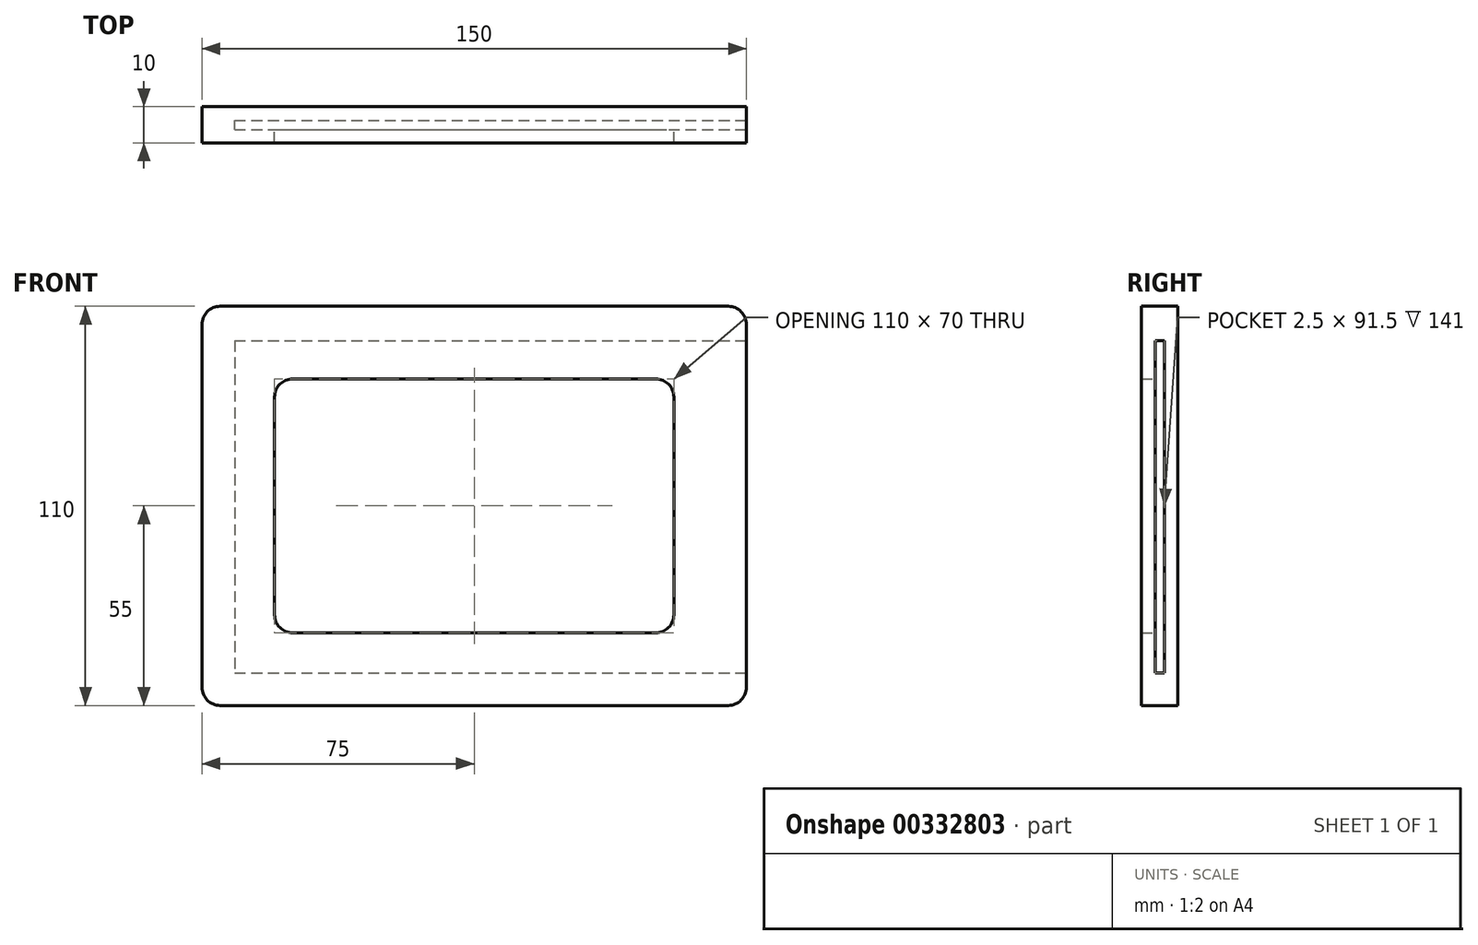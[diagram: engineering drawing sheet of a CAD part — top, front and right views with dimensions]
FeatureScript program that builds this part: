
annotation { "Feature Type Name" : "Feature", "Feature Type Description" : "" }
export const myFeature = defineFeature(function(context is Context, id is Id, definition is map)
    precondition{}
    {
        {
            var Q0;
            Q0=qCreatedBy(makeId("Front.planeOp"),FACE);
            var sketch = newSketch(context, id + "F0", { "sketchPlane" : qUnion([Q0])});
            skLineSegment(sketch, "E0.bottom", {"start": v(65, 45) * mm, "end": v(-65, 45) * mm, "construction": true});
            skLineSegment(sketch, "E0.top", {"start": v(65, -45) * mm, "end": v(-65, -45) * mm, "construction": true});
            skLineSegment(sketch, "E0.left", {"start": v(65, 45) * mm, "end": v(65, -45) * mm, "construction": true});
            skLineSegment(sketch, "E0.right", {"start": v(-65, 45) * mm, "end": v(-65, -45) * mm, "construction": true});
            skPoint(sketch, "E0.middle", {"position": v(0, 0) * mm});
            skLineSegment(sketch, "E1.bottom", {"start": v(75, 55) * mm, "end": v(-75, 55) * mm});
            skLineSegment(sketch, "E1.top", {"start": v(75, -55) * mm, "end": v(-75, -55) * mm});
            skLineSegment(sketch, "E1.left", {"start": v(75, 55) * mm, "end": v(75, -55) * mm});
            skLineSegment(sketch, "E1.right", {"start": v(-75, 55) * mm, "end": v(-75, -55) * mm});
            skLineSegment(sketch, "E2.bottom", {"start": v(-66, 45.5) * mm, "end": v(75, 45.5) * mm});
            skLineSegment(sketch, "E2.top", {"start": v(-66, -46) * mm, "end": v(75, -46) * mm});
            skLineSegment(sketch, "E2.left", {"start": v(-66, 45.5) * mm, "end": v(-66, -46) * mm});
            skLineSegment(sketch, "E2.right", {"start": v(75, 45.5) * mm, "end": v(75, -46) * mm});
            skLineSegment(sketch, "E3.bottom", {"start": v(55, 35) * mm, "end": v(-55, 35) * mm});
            skLineSegment(sketch, "E3.top", {"start": v(55, -35) * mm, "end": v(-55, -35) * mm});
            skLineSegment(sketch, "E3.left", {"start": v(55, 35) * mm, "end": v(55, -35) * mm});
            skLineSegment(sketch, "E3.right", {"start": v(-55, 35) * mm, "end": v(-55, -35) * mm});
            skSolve(sketch);
        }
        {
            var Q0;
            {var subQ4=sQuery(id+"F0.wireOp",EDGE,"E1.bottom");Q0=makeQuery(id+"F0.imprint","IMPRINT",FACE,{"disambiguationData":[TD([[makeQuery(id+"F0.imprint","IMPRINT",EDGE,{"derivedFrom":subQ4}),1.0]])]});}
            var Q1;
            Q1=makeQuery(id+"F0.imprint","IMPRINT",FACE,{"disambiguationData":[TD([[makeQuery(id+"F0.imprint","IMPRINT",EDGE,{"derivedFrom":sQuery(id+"F0.wireOp",EDGE,"E2.bottom")}),-1.0]])]});
            var Q2;
            Q2=makeQuery(id+"F0.imprint","IMPRINT",FACE,{"disambiguationData":[TD([[makeQuery(id+"F0.imprint","IMPRINT",EDGE,{"derivedFrom":sQuery(id+"F0.wireOp",EDGE,"E3.bottom")}),1.0]])]});
            extrude(context, id + "F1", {"entities" : qUnion([Q0, Q1, Q2]), "endBound" : BoundingType.SYMMETRIC, "depth" : 10 * mm});
        }
        {
            var Q0;
            Q0=makeQuery(id+"F0.imprint","IMPRINT",FACE,{"disambiguationData":[TD([[makeQuery(id+"F0.imprint","IMPRINT",EDGE,{"derivedFrom":sQuery(id+"F0.wireOp",EDGE,"E2.bottom")}),-1.0]])]});
            var Q1;
            Q1=makeQuery(id+"F0.imprint","IMPRINT",FACE,{"disambiguationData":[TD([[makeQuery(id+"F0.imprint","IMPRINT",EDGE,{"derivedFrom":sQuery(id+"F0.wireOp",EDGE,"E3.bottom")}),1.0]])]});
            extrude(context, id + "F2", {"entities" : qUnion([Q0, Q1]), "operationType" : NewBodyOperationType.REMOVE, "endBound" : BoundingType.SYMMETRIC, "depth" : 2.5 * mm});
        }
        {
            var Q0;
            Q0=makeQuery(id+"F0.imprint","IMPRINT",FACE,{"disambiguationData":[TD([[makeQuery(id+"F0.imprint","IMPRINT",EDGE,{"derivedFrom":sQuery(id+"F0.wireOp",EDGE,"E3.bottom")}),1.0]])]});
            extrude(context, id + "F3", {"entities" : qUnion([Q0]), "operationType" : NewBodyOperationType.REMOVE, "endBound" : BoundingType.THROUGH_ALL, "depth" : 2.5 * mm});
        }
        {
            var Q0;
            Q0=makeQuery(id+"F1.opExtrude","SWEPT_EDGE",EDGE,{"disambiguationData":[OSD([sQuery(id+"F0.wireOp",EDGE,"E1.bottom"),sQuery(id+"F0.wireOp",EDGE,"E1.right")])]});
            var Q1;
            Q1=makeQuery(id+"F1.opExtrude","SWEPT_EDGE",EDGE,{"disambiguationData":[OSD([sQuery(id+"F0.wireOp",EDGE,"E1.bottom"),sQuery(id+"F0.wireOp",EDGE,"E1.left")])]});
            var Q2;
            Q2=makeQuery(id+"F1.opExtrude","SWEPT_EDGE",EDGE,{"disambiguationData":[OSD([sQuery(id+"F0.wireOp",EDGE,"E1.top"),sQuery(id+"F0.wireOp",EDGE,"E1.left")])]});
            var Q3;
            Q3=makeQuery(id+"F1.opExtrude","SWEPT_EDGE",EDGE,{"disambiguationData":[OSD([sQuery(id+"F0.wireOp",EDGE,"E1.top"),sQuery(id+"F0.wireOp",EDGE,"E1.right")])]});
            fillet(context, id + "F4", {"entities" : qUnion([Q0, Q1, Q2, Q3]), "radius" : 5 * mm, "tangentPropagation" : true, "allowEdgeOverflow" : false});
        }
        {
            var Q0;
            Q0=makeQuery(id+"F3.boolean.opBoolean","COPY",EDGE,{"derivedFrom":makeQuery(id+"F3.opExtrude","SWEPT_EDGE",EDGE,{"disambiguationData":[OSD([sQuery(id+"F0.wireOp",EDGE,"E3.bottom"),sQuery(id+"F0.wireOp",EDGE,"E3.right")])]})});
            var Q1;
            Q1=makeQuery(id+"F3.boolean.opBoolean","COPY",EDGE,{"derivedFrom":makeQuery(id+"F3.opExtrude","SWEPT_EDGE",EDGE,{"disambiguationData":[OSD([sQuery(id+"F0.wireOp",EDGE,"E3.bottom"),sQuery(id+"F0.wireOp",EDGE,"E3.left")])]})});
            var Q2;
            Q2=makeQuery(id+"F3.boolean.opBoolean","COPY",EDGE,{"derivedFrom":makeQuery(id+"F3.opExtrude","SWEPT_EDGE",EDGE,{"disambiguationData":[OSD([sQuery(id+"F0.wireOp",EDGE,"E3.top"),sQuery(id+"F0.wireOp",EDGE,"E3.left")])]})});
            var Q3;
            Q3=makeQuery(id+"F3.boolean.opBoolean","COPY",EDGE,{"derivedFrom":makeQuery(id+"F3.opExtrude","SWEPT_EDGE",EDGE,{"disambiguationData":[OSD([sQuery(id+"F0.wireOp",EDGE,"E3.top"),sQuery(id+"F0.wireOp",EDGE,"E3.right")])]})});
            fillet(context, id + "F5", {"entities" : qUnion([Q0, Q1, Q2, Q3]), "radius" : 5 * mm, "tangentPropagation" : true, "allowEdgeOverflow" : false});
        }
    });
